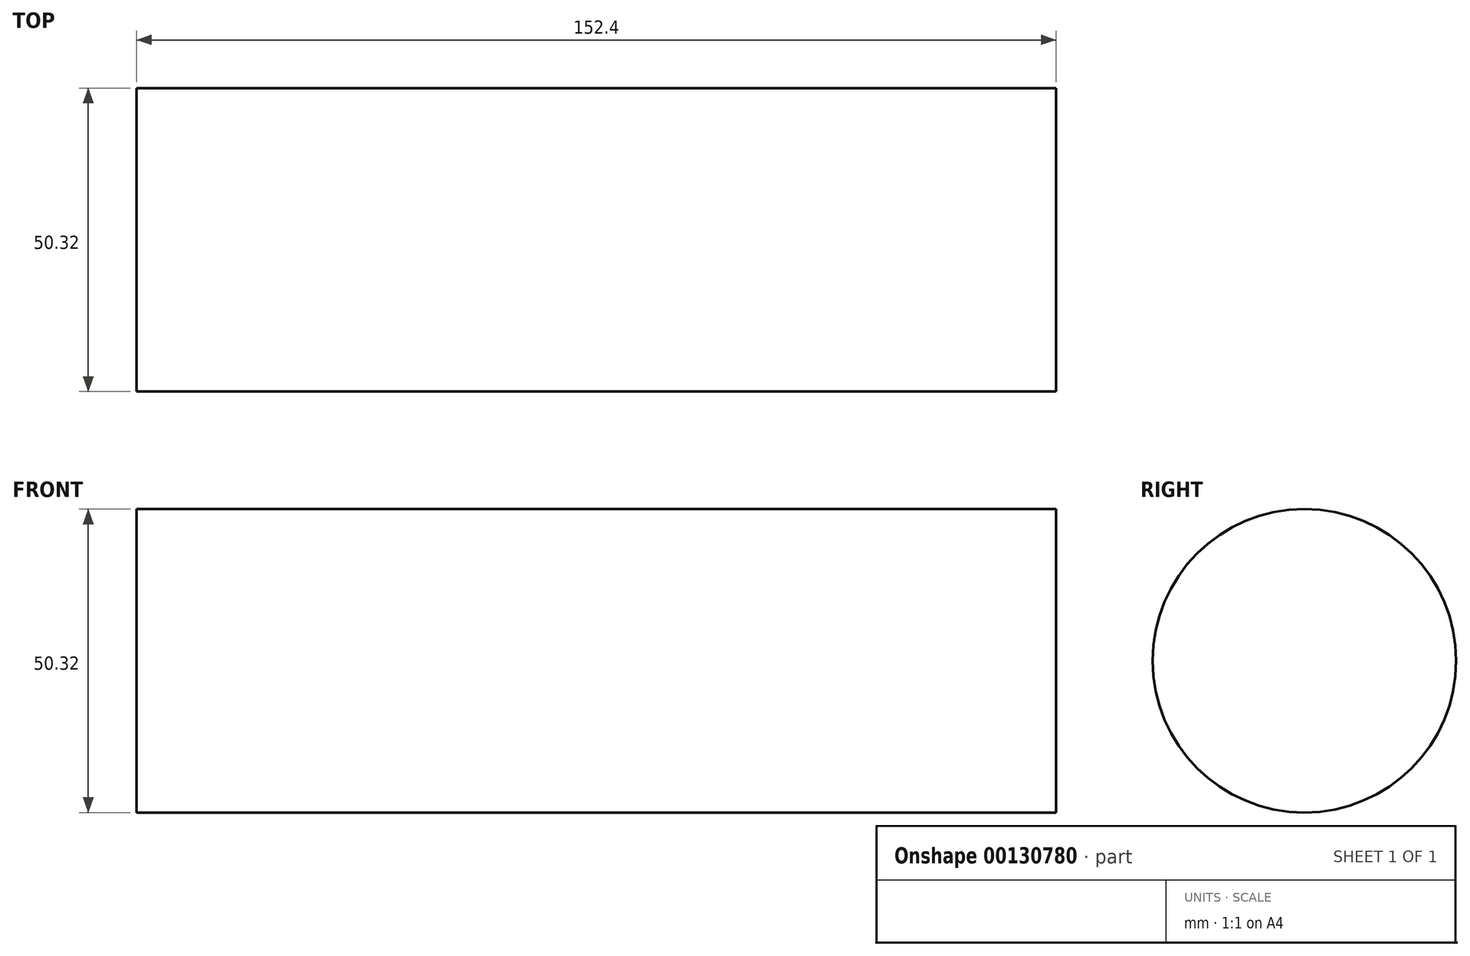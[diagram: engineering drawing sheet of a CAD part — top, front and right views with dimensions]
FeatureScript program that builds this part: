
annotation { "Feature Type Name" : "Feature", "Feature Type Description" : "" }
export const myFeature = defineFeature(function(context is Context, id is Id, definition is map)
    precondition{}
    {
        {
            var Q0;
            Q0=qCreatedBy(makeId("Right.planeOp"),FACE);
            var sketch = newSketch(context, id + "F0", { "sketchPlane" : qUnion([Q0])});
            skCircle(sketch, "E0", {"center": v(0, 0) * mm, "radius": 25.16 * mm});
            skSolve(sketch);
        }
        {
            var Q0;
            Q0=makeQuery(id+"F0.imprint","IMPRINT",FACE,{"disambiguationData":[TD([[makeQuery(id+"F0.imprint","IMPRINT",EDGE,{"derivedFrom":sQuery(id+"F0.wireOp",EDGE,"E0")}),1.0]])]});
            extrude(context, id + "F1", {"entities" : qUnion([Q0]), "oppositeDirection" : true, "depth" : 152.4 * mm});
        }
    });
